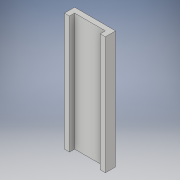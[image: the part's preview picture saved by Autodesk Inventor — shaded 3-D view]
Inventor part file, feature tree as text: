
AUTODESK INVENTOR PART (.ipt)
format: ipt  version: 2017 (Build 210142000, 142)  size: 106,496 bytes
history: native  units: in
note: dims shown in document units (in); Inventor stores cm internally (conversion verified against a paired STEP export)
features: extrude x2, sketch x2
ambient origin geometry x8: Origin, YZ Plane, XZ Plane, XY Plane, X Axis, Y Axis, Z Axis, Center Point
bodies: Solid1 (feature_tree)
feature tree (4):
  extrude  "Extrusion1"  Depth=23.0in
  extrude  "Extrusion2"  Depth=1.0in
  sketch  "Sketch1"  dims[d0=8.0in d1=23.0in]
  sketch  "Sketch2"  dims[d2=1.0in d3=0.0in d4=1.0in d5=1.0in d6=23.0in d7=1.0in d8=0.0in]
